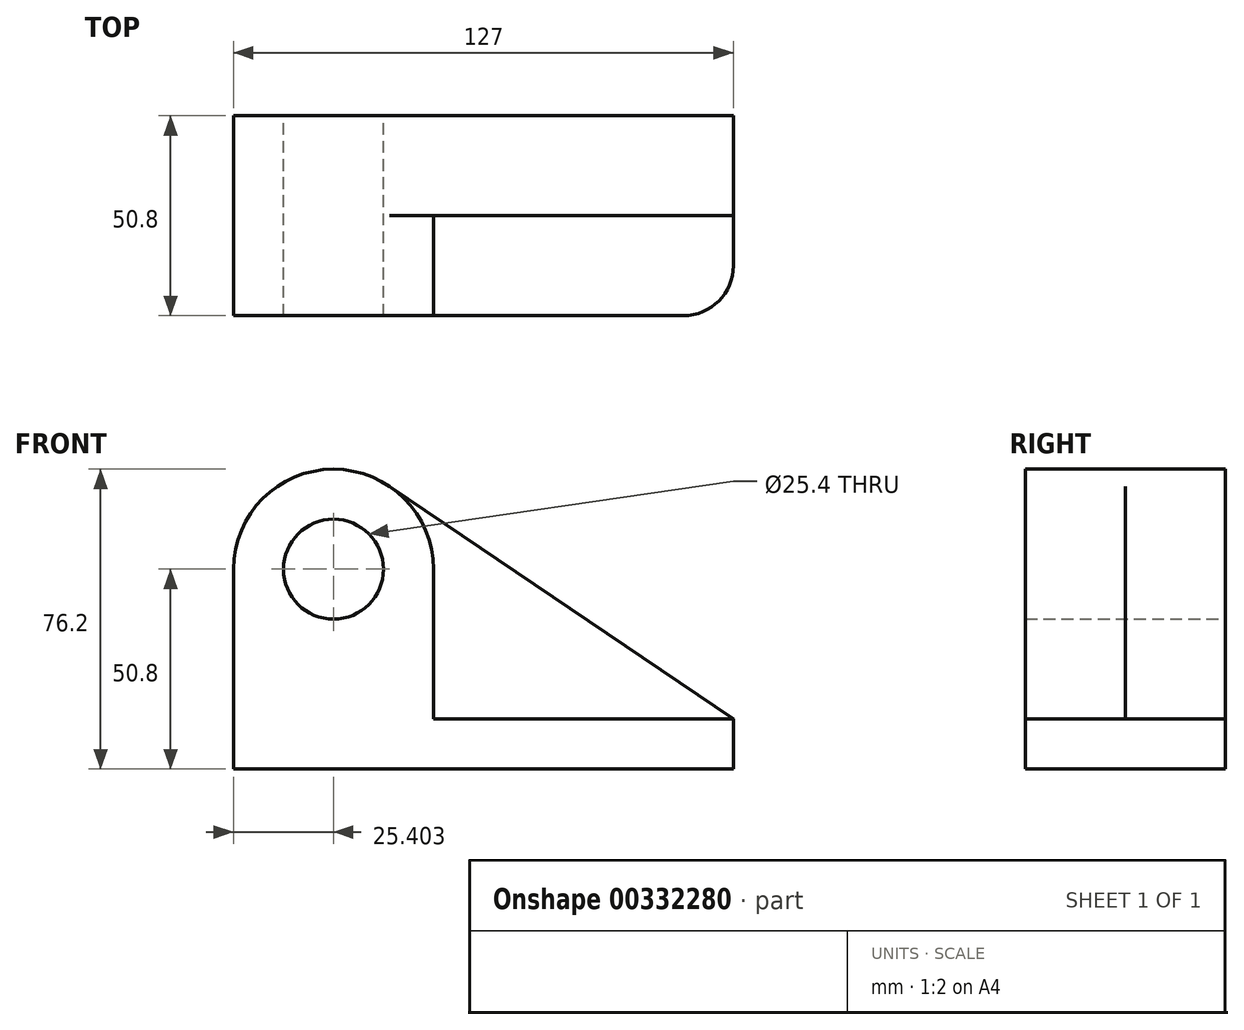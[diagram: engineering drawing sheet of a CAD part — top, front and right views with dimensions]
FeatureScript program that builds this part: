
annotation { "Feature Type Name" : "Feature", "Feature Type Description" : "" }
export const myFeature = defineFeature(function(context is Context, id is Id, definition is map)
    precondition{}
    {
        {
            var Q0;
            Q0=qCreatedBy(makeId("Front.planeOp"),FACE);
            var sketch = newSketch(context, id + "F0", { "sketchPlane" : qUnion([Q0])});
            skCircle(sketch, "E0", {"center": v(-42.19, 50.8) * mm, "radius": 12.7 * mm});
            skArc(sketch, "E1", {"start": v(-27.95, 71.83) * mm, "mid": v(-54.1, 73.24) * mm, "end": v(-67.59, 50.8) * mm});
            skLineSegment(sketch, "E2", {"start": v(-67.59, 50.8) * mm, "end": v(-67.59, 0) * mm});
            skLineSegment(sketch, "E3", {"start": v(-67.59, 0) * mm, "end": v(59.41, 0) * mm});
            skLineSegment(sketch, "E4", {"start": v(59.41, 0) * mm, "end": v(59.41, 12.7) * mm});
            skLineSegment(sketch, "E5", {"start": v(59.41, 12.7) * mm, "end": v(-27.95, 71.83) * mm});
            skSolve(sketch);
        }
        {
            var Q0;
            Q0 = qSketchRegion(id + "F0", true);
            extrude(context, id + "F1", {"entities" : qUnion([Q0]), "depth" : 25.4 * mm});
        }
        {
            var Q0;
            Q0=makeQuery(id+"F1.opExtrude","CAP_FACE",FACE,{"disambiguationData":[OSD([sQuery(id+"F0.wireOp",EDGE,"E0"),sQuery(id+"F0.wireOp",EDGE,"E1"),sQuery(id+"F0.wireOp",EDGE,"E2"),sQuery(id+"F0.wireOp",EDGE,"E3"),sQuery(id+"F0.wireOp",EDGE,"E4"),sQuery(id+"F0.wireOp",EDGE,"E5")])],"isStart":false});
            var sketch = newSketch(context, id + "F2", { "sketchPlane" : qUnion([Q0])});
            skArc(sketch, "E6", {"start": v(-16.79, 50.8) * mm, "mid": v(-42.19, 76.2) * mm, "end": v(-67.59, 50.8) * mm});
            skLineSegment(sketch, "E7.bottom", {"start": v(59.41, 12.7) * mm, "end": v(-16.79, 12.7) * mm});
            skLineSegment(sketch, "E7.top", {"start": v(59.41, 0) * mm, "end": v(-67.59, 0) * mm});
            skLineSegment(sketch, "E7.left", {"start": v(59.41, 12.7) * mm, "end": v(59.41, 0) * mm});
            skCircle(sketch, "E8", {"center": v(-42.19, 50.8) * mm, "radius": 12.7 * mm});
            skLineSegment(sketch, "E9", {"start": v(-67.59, 50.8) * mm, "end": v(-67.59, 12.7) * mm});
            skLineSegment(sketch, "E10", {"start": v(-16.79, 50.8) * mm, "end": v(-16.79, 12.7) * mm});
            skPoint(sketch, "E11.orphan", {"position": v(-16.79, 0) * mm});
            skSolve(sketch);
        }
        {
            var Q0;
            Q0=makeQuery(id+"F2.imprint","IMPRINT",FACE,{"disambiguationData":[TD([[makeQuery(id+"F2.imprint","IMPRINT",EDGE,{"derivedFrom":sQuery(id+"F2.wireOp",EDGE,"E7.bottom")}),1.0]])]});
            extrude(context, id + "F3", {"entities" : qUnion([Q0]), "operationType" : NewBodyOperationType.ADD, "depth" : 25.4 * mm});
        }
        {
            var Q0;
            Q0=makeQuery(id+"F3.opExtrude","CAP_EDGE",EDGE,{"disambiguationData":[OSD([sQuery(id+"F2.wireOp",EDGE,"E7.left")])],"isStart":false});
            fillet(context, id + "F4", {"entities" : qUnion([Q0]), "radius" : 12.7 * mm, "tangentPropagation" : true, "allowEdgeOverflow" : false});
        }
    });
